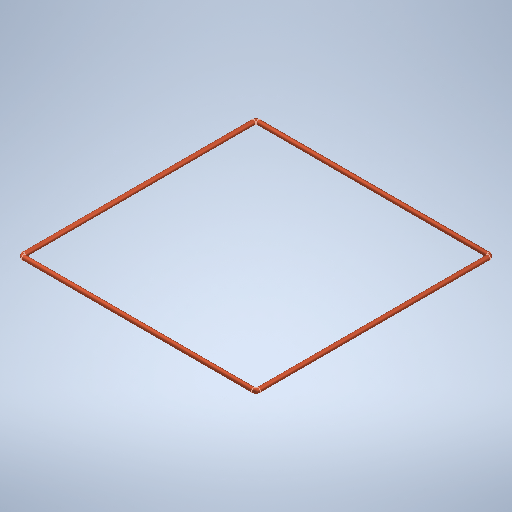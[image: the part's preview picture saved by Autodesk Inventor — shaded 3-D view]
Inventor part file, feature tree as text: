
AUTODESK INVENTOR PART (.ipt)
format: ipt  version: 2025 (Build 290162010, 162A)  size: 279,040 bytes
history: native  units: in
note: dims shown in document units (in); Inventor stores cm internally (conversion verified against a paired STEP export)
features: sketch x2, plane x1, sweep x1
ambient origin geometry x8: Origin, YZ Plane, XZ Plane, XY Plane, X Axis, Y Axis, Z Axis, Center Point
bodies: Solid1 (feature_tree)
feature tree (4):
  sketch  "Sketch1"  dims[d1=0.1022in d2=0.1022in]
  plane  "Work Plane1"
  sweep  "Sweep1"
  sketch  "Sketch2"  dims[d3=0.1022in d4=0.1022in d5=0.1022in d7=10.5in d8=0.1022in d9=0.2043in d10=0.0in d11=0.0in]
